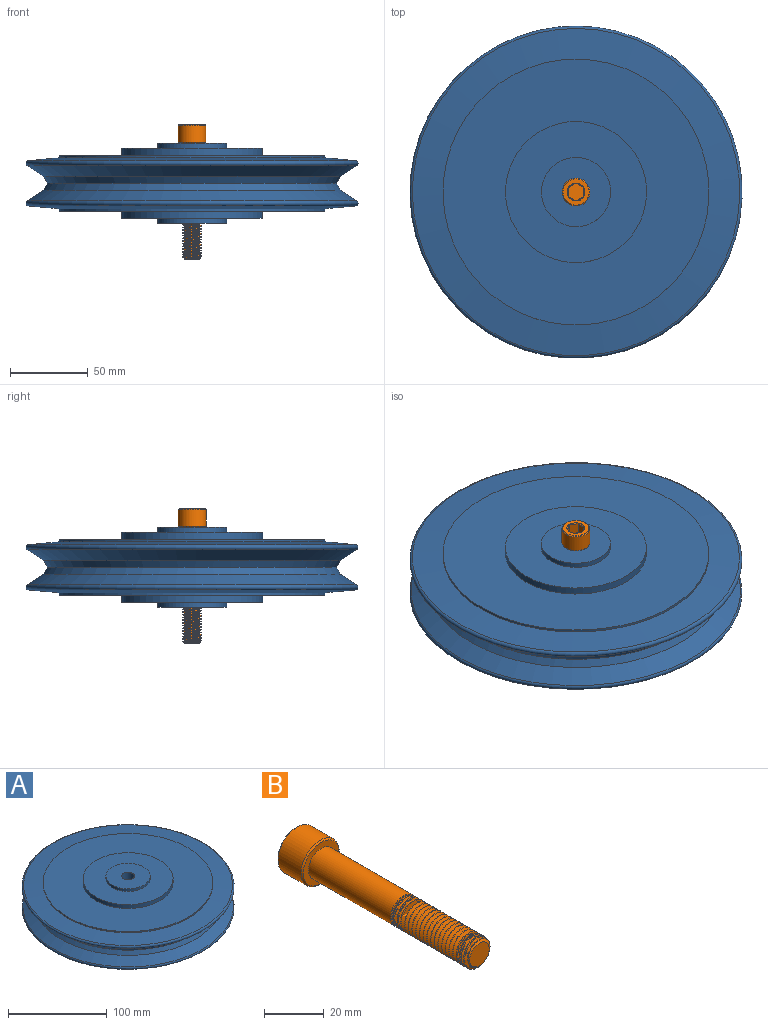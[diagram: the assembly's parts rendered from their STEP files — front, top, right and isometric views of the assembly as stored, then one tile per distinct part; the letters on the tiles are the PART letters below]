
ASSEMBLY  parts=2 mates=1
PART A: 21 faces, bbox 232x232x51.8 mm
  f0: cone r=95.85mm half-angle=30.9deg, axis (0,0,1), area 3126.7mm2, adj f1,f11
  f1: cone r=106.37mm half-angle=56.8deg, axis (0,0,1), area 7982.9mm2, adj f0,f2
  f2: torus R=105.41mm, axis (0,0,1), area 2884.1mm2, adj f1,f3
  f3: cone r=85.78mm half-angle=84.8deg, axis (0,0,-1), area 11947.7mm2, adj f2,f4
  f4: cylinder r=85.78mm len=171.55mm, axis (0,0,1), area 820.4mm2, adj f3,f5
  f5: plane 171.55x171.55mm, normal (0,0,1), area 16606.3mm2, adj f4,f6
  f6: cylinder r=45.52mm len=91.03mm, axis (0,0,1), area 1346.2mm2, adj f5,f7
  f7: plane 91.03x91.03mm, normal (0,0,1), area 4941mm2, adj f6,f8
  f8: cylinder r=22.34mm len=44.68mm, axis (0,0,1), area 457.4mm2, adj f7,f9
  f9: plane 44.68x44.68mm, normal (0,0,1), area 1435.3mm2, adj f8,f10
  f10: cylinder r=6.49mm len=51.76mm, axis (0,0,1), area 2110.1mm2, adj f9,f20
  f11: cone r=95.85mm half-angle=30.9deg, axis (0,0,-1), area 3126.7mm2, adj f0,f12
  f12: cone r=106.37mm half-angle=56.8deg, axis (0,0,-1), area 7982.9mm2, adj f11,f13
  f13: torus R=105.41mm, axis (0,0,-1), area 2884.1mm2, adj f12,f14
  f14: cone r=85.78mm half-angle=84.8deg, axis (0,0,1), area 11947.7mm2, adj f13,f15
  f15: cylinder r=85.78mm len=171.55mm, axis (0,0,-1), area 820.4mm2, adj f14,f16
  f16: plane 171.55x171.55mm, normal (0,0,-1), area 16606.3mm2, adj f15,f17
  f17: cylinder r=45.52mm len=91.03mm, axis (0,0,-1), area 1346.2mm2, adj f16,f18
  f18: plane 91.03x91.03mm, normal (0,0,-1), area 4941mm2, adj f17,f19
  f19: cylinder r=22.34mm len=44.68mm, axis (0,0,-1), area 457.4mm2, adj f18,f20
  f20: plane 44.68x44.68mm, normal (0,0,-1), area 1435.3mm2, adj f10,f19
PART B: 46 faces, bbox 18.6x88x18.6 mm
  f0: cone r=9mm half-angle=45deg, axis (0,1,0), area 41.9mm2, adj f3,f33
  f1: cone r=8.46mm half-angle=45deg, axis (0,-1,0), area 41.9mm2, adj f3,f32
  f2: cone r=5.77mm half-angle=45deg, axis (0,1,0), area 3.2mm2, adj f32,f44
  f3: cylinder r=9mm len=18mm, axis (0,-1,0), area 617.5mm2, adj f0,f1
  f4: cone r=6mm half-angle=70deg, axis (0,1,0), area 9.9mm2, adj f26,f28,f29,f31
  f5: cone r=4.61mm half-angle=55deg, axis (0,1,0), area 32.3mm2, adj f7,f27,f28,f29,f30
  f6: cylinder r=6mm len=12mm, axis (0,-1,0), area 8.2mm2, adj f7,f8,f28,f29
  f7: cylinder r=6mm len=8.53mm, axis (0,-1,0), area 2.1mm2, adj f5,f6,f28,f29
  f8: cylinder r=6mm len=12mm, axis (0,-1,0), area 8.2mm2, adj f6,f9,f28,f29
  f9: cylinder r=6mm len=12mm, axis (0,-1,0), area 8.2mm2, adj f8,f10,f28,f29
  f10: cylinder r=6mm len=12mm, axis (0,-1,0), area 8.2mm2, adj f9,f11,f28,f29
  f11: cylinder r=6mm len=12mm, axis (0,-1,0), area 8.2mm2, adj f10,f12,f28,f29
  f12: cylinder r=6mm len=12mm, axis (0,-1,0), area 8.2mm2, adj f11,f13,f28,f29
  f13: cylinder r=6mm len=12mm, axis (0,-1,0), area 8.2mm2, adj f12,f14,f28,f29
  f14: cylinder r=6mm len=12mm, axis (0,-1,0), area 8.2mm2, adj f13,f15,f28,f29
  f15: cylinder r=6mm len=12mm, axis (0,-1,0), area 8.2mm2, adj f14,f16,f28,f29
  f16: cylinder r=6mm len=12mm, axis (0,-1,0), area 8.2mm2, adj f15,f17,f28,f29
  f17: cylinder r=6mm len=12mm, axis (0,-1,0), area 8.2mm2, adj f16,f18,f28,f29
  f18: cylinder r=6mm len=12mm, axis (0,-1,0), area 8.2mm2, adj f17,f19,f28,f29
  f19: cylinder r=6mm len=12mm, axis (0,-1,0), area 8.2mm2, adj f18,f20,f28,f29
  f20: cylinder r=6mm len=12mm, axis (0,-1,0), area 8.2mm2, adj f19,f21,f28,f29
  f21: cylinder r=6mm len=12mm, axis (0,-1,0), area 8.2mm2, adj f20,f22,f28,f29
  f22: cylinder r=6mm len=12mm, axis (0,-1,0), area 8.2mm2, adj f21,f23,f28,f29
  f23: cylinder r=6mm len=12mm, axis (0,-1,0), area 8.2mm2, adj f22,f24,f28,f29
  f24: cylinder r=6mm len=12mm, axis (0,-1,0), area 8.2mm2, adj f23,f25,f28,f29
  f25: cylinder r=6mm len=12mm, axis (0,-1,0), area 8.2mm2, adj f24,f26,f28,f29
  f26: cylinder r=6mm len=40.44mm, axis (0,-1,0), area 1472.5mm2, adj f4,f25,f28,f29,f33
  f27: cylinder r=4.86mm len=35.82mm, axis (0,1,0), area 136.8mm2, adj f5,f28,f29,f31
  f28: bspline ~37.26x11.97mm, area 907.9mm2, adj f4,f5,f6,f7,f8,f9,f10,f11
  f29: bspline ~36.48x12mm, area 907.7mm2, adj f4,f5,f6,f7,f8,f9,f10,f11
  f30: plane 9.22x9.22mm, normal (0,-1,0), area 66.7mm2, adj f5
  f31: plane 11.73x9.03mm, normal (0,-1,0), area 10.6mm2, adj f4,f27,f28,f29
  f32: plane 16.92x16.92mm, normal (0,1,0), area 120.1mm2, adj f1,f2,f34,f35,f36,f37,f38
  f33: plane 16.92x16.92mm, normal (0,-1,0), area 111.8mm2, adj f0,f26
  f34: cone r=5.77mm half-angle=45deg, axis (0,1,0), area 4.3mm2, adj f32,f40
  f35: cone r=5.77mm half-angle=45deg, axis (0,1,0), area 4.3mm2, adj f32,f41
  f36: cone r=5.77mm half-angle=45deg, axis (0,1,0), area 4.3mm2, adj f32,f42
  f37: cone r=5.77mm half-angle=45deg, axis (0,1,0), area 4.3mm2, adj f32,f43
  f38: cone r=5.77mm half-angle=45deg, axis (0,1,0), area 4.3mm2, adj f32,f45
  f39: plane 11.55x10mm, normal (0,1,0), area 86.6mm2, adj f40,f41,f42,f43,f44,f45
  f40: plane 7.5x5mm, normal (-0.5,0,-0.87), area 40.3mm2, adj f34,f39,f41,f45
  f41: plane 7.5x5.77mm, normal (-1,0,0), area 40.4mm2, adj f35,f39,f40,f42
  f42: plane 7.5x5mm, normal (-0.5,0,0.87), area 40.3mm2, adj f36,f39,f41,f43
  f43: plane 7.5x5mm, normal (0.5,0,0.87), area 40.4mm2, adj f37,f39,f42,f44
  f44: plane 8.06x6.34mm, normal (1,0,0), area 40.4mm2, adj f2,f39,f43,f45
  f45: plane 7.5x5mm, normal (0.5,0,-0.87), area 40.4mm2, adj f38,f39,f40,f44
PLACE A rot(axis=(0,0,1),61.3deg) t=(-54.43,-99.53,24.52)mm
PLACE B rot(axis=(1,0,0),90deg) t=(0,0,-75.54)mm
MATE revolute B.f0 <-> A.f0  axis (0,0,-1) through (0,0,-0.54)mm
